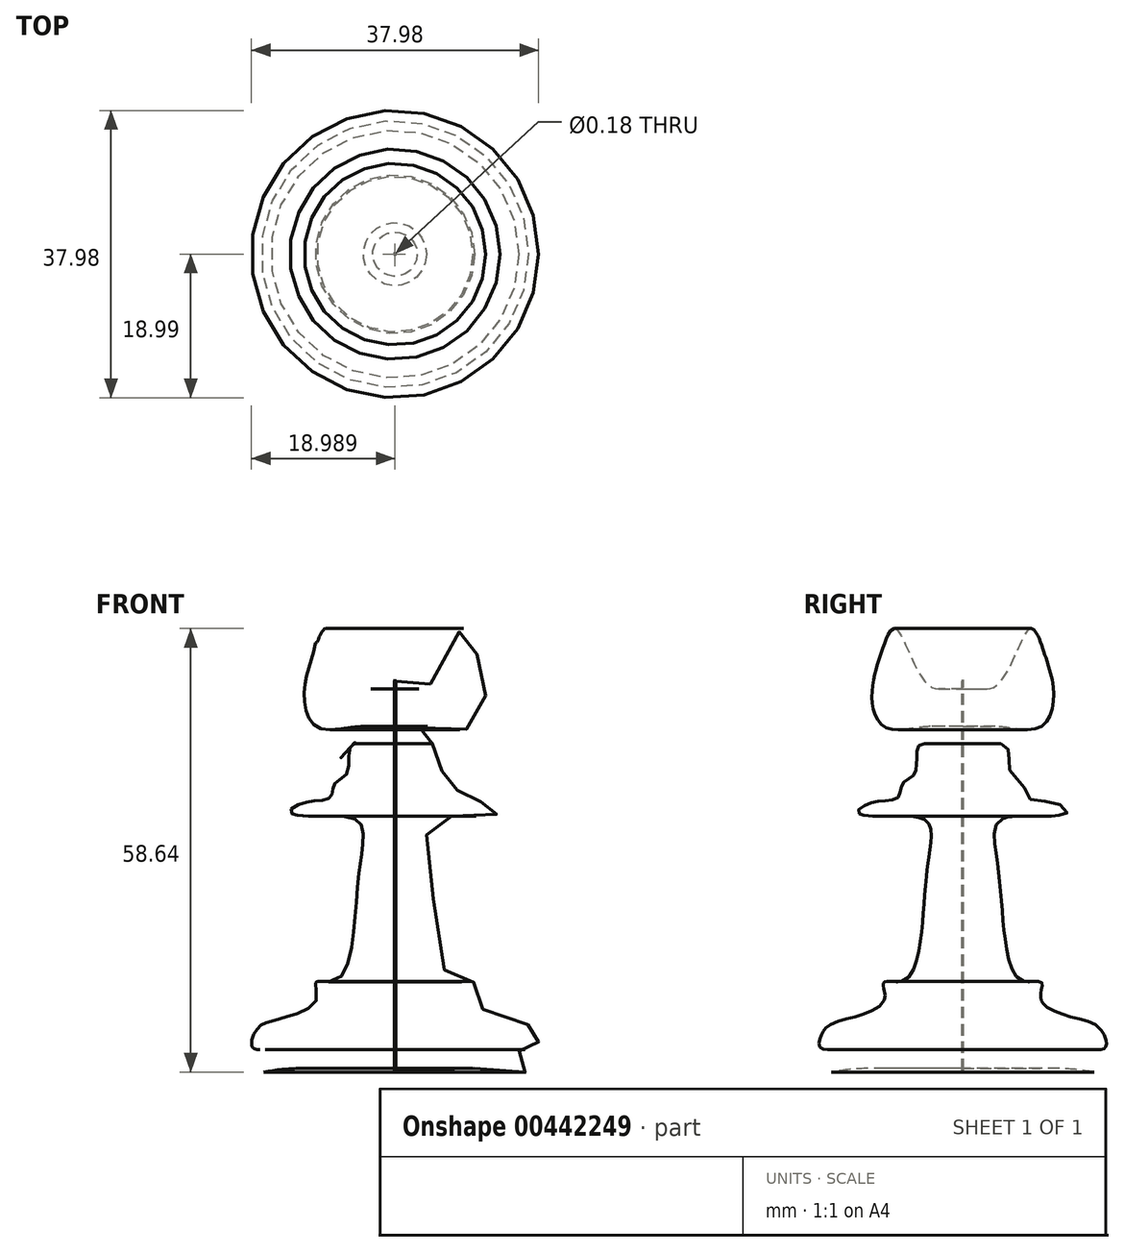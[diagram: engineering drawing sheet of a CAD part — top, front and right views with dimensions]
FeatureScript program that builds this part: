
annotation { "Feature Type Name" : "Feature", "Feature Type Description" : "" }
export const myFeature = defineFeature(function(context is Context, id is Id, definition is map)
    precondition{}
    {
        {
            var Q0;
            Q0=qCreatedBy(makeId("Front.planeOp"),FACE);
            var sketch = newSketch(context, id + "F0", { "sketchPlane" : qUnion([Q0])});
            skFitSpline(sketch, "E0", {"points": [v(0, 0) * mm, v(-15.69, 0) * mm, v(-17.57, 0) * mm, v(-16.32, 2.51) * mm, v(-18.51, 2.82) * mm, v(-18.83, 4.08) * mm, v(-18.2, 5.33) * mm, v(-16.94, 6.28) * mm, v(-10.35, 9.1) * mm, v(-10.35, 11.6) * mm, v(-7.53, 11.92) * mm, v(-4.7, 25.73) * mm, v(-4.7, 32.95) * mm, v(-10.67, 33.57) * mm, v(-13.8, 34.2) * mm, v(-11.6, 35.46) * mm, v(-8.47, 36.08) * mm, v(-7.84, 37.97) * mm, v(-6.28, 39.22) * mm, v(-5.65, 42.99) * mm, v(-3.45, 43.3) * mm, v(-3.14, 45.18) * mm, v(-9.73, 45.18) * mm, v(-11.92, 49.57) * mm, v(-10.67, 55.22) * mm, v(-8.79, 58.36) * mm, v(-3.77, 50.52) * mm, v(0, 51.46) * mm, v(0, 51.14) * mm, v(-6.59, 60.24) * mm, v(-3.45, 62.44) * mm, v(-6.28, 63.07) * mm, v(-6.9, 65.9) * mm, v(-4.4, 67.46) * mm, v(0, 67.46) * mm, v(0, 68.09) * mm], "startDerivative": vector(-317.48, 12.3) * mm, "endDerivative": vector(-22.72, 63.76) * mm});
            skLineSegment(sketch, "E1", {"start": v(0, 67.46) * mm, "end": v(0, 0) * mm});
            skLineSegment(sketch, "E2", {"start": v(0.09, 74.36) * mm, "end": v(0.09, -21.65) * mm, "construction": true});
            skSolve(sketch);
        }
        {
            var Q0;
            {var subQ0=sQuery(id+"F0.wireOp",EDGE,"E1");var subQ1=sQuery(id+"F0.wireOp",EDGE,"E0");var subQ2=makeQuery(id+"F0.imprint","INTERSECT",VERTEX,{"disambiguationData":[OD(0.0)],"derivedFrom":[subQ1,subQ0]});Q0=makeQuery(id+"F0.imprint","IMPRINT",FACE,{"disambiguationData":[TD([[makeQuery(id+"F0.imprint","IMPRINT",EDGE,{"disambiguationData":[TD([[subQ2,-1.0]])],"derivedFrom":subQ1}),-1.0]])]});}
            var Q1;
            Q1=sQuery(id+"F0.wireOp",EDGE,"E2");
            revolve(context, id + "F1", {"entities" : qUnion([Q0]), "axis" : qUnion([Q1]), "revolveType" : RevolveType.FULL});
        }
    });
